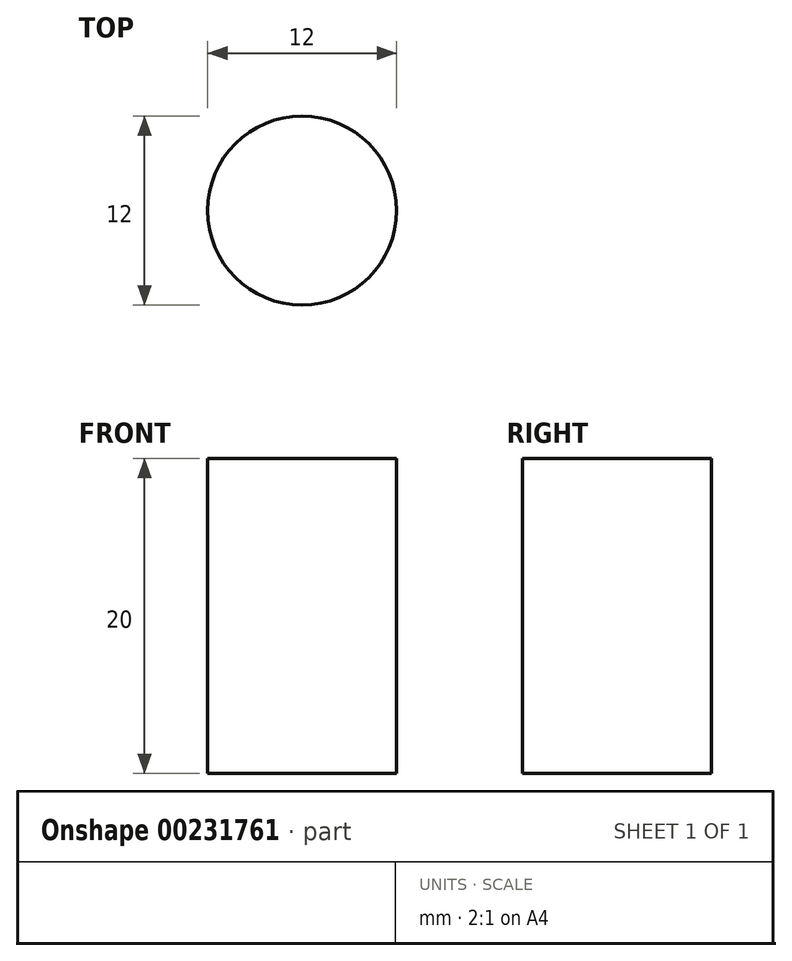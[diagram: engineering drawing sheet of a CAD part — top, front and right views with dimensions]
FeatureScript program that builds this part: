
annotation { "Feature Type Name" : "Feature", "Feature Type Description" : "" }
export const myFeature = defineFeature(function(context is Context, id is Id, definition is map)
    precondition{}
    {
        {
            var Q0;
            Q0=qCreatedBy(makeId("Top.planeOp"),FACE);
            var sketch = newSketch(context, id + "F0", { "sketchPlane" : qUnion([Q0])});
            skCircle(sketch, "E0", {"center": v(0, 0) * mm, "radius": 6 * mm});
            skSolve(sketch);
        }
        {
            var Q0;
            Q0 = qSketchRegion(id + "F0", true);
            var Q1;
            Q1 = qConstructionFilter(qBodyType(qCreatedBy(id + "F0" ,EDGE), BodyType.WIRE), ConstructionObject.NO);
            extrude(context, id + "F1", {"entities" : qUnion([Q0]), "bodyType" : ToolBodyType.SURFACE, "operationType" : NewBodyOperationType.ADD, "surfaceEntities" : qUnion([Q1]), "depth" : 20 * mm});
        }
    });
